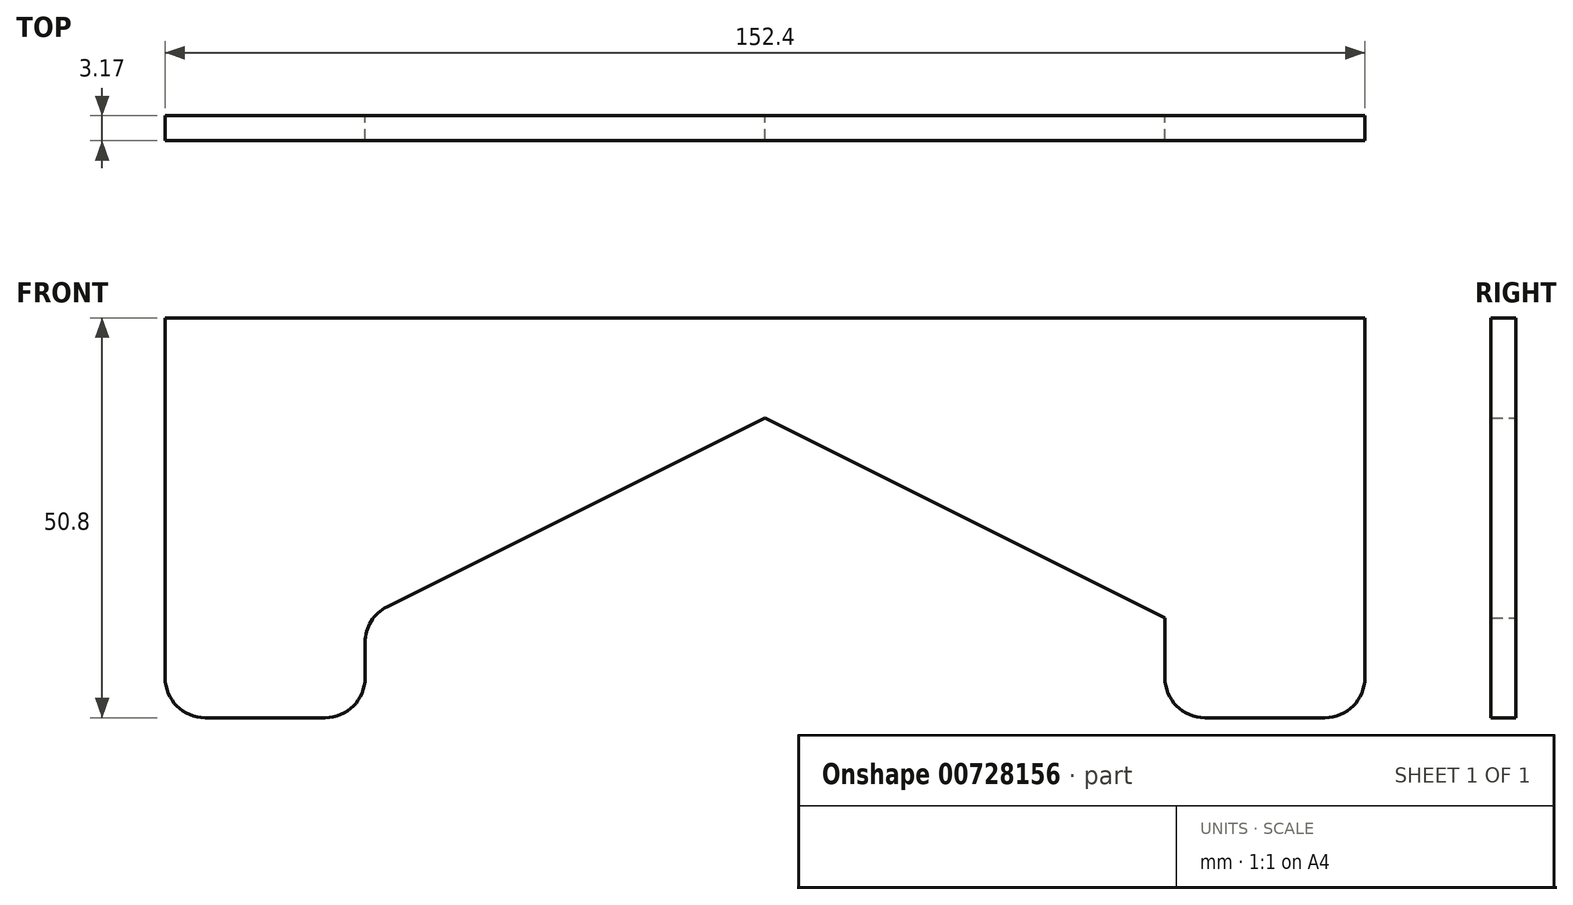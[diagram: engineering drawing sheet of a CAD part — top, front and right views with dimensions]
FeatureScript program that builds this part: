
annotation { "Feature Type Name" : "Feature", "Feature Type Description" : "" }
export const myFeature = defineFeature(function(context is Context, id is Id, definition is map)
    precondition{}
    {
        {
            var Q0;
            Q0=qCreatedBy(makeId("Front.planeOp"),FACE);
            var sketch = newSketch(context, id + "F0", { "sketchPlane" : qUnion([Q0])});
            skLineSegment(sketch, "E0", {"start": v(-107.22, 19.05) * mm, "end": v(-107.22, -31.75) * mm});
            skLineSegment(sketch, "E1", {"start": v(-107.22, -31.75) * mm, "end": v(45.18, -31.75) * mm});
            skLineSegment(sketch, "E2", {"start": v(45.18, -31.75) * mm, "end": v(45.18, 19.05) * mm});
            skLineSegment(sketch, "E3", {"start": v(45.18, 19.05) * mm, "end": v(-107.22, 19.05) * mm});
            skLineSegment(sketch, "E4", {"start": v(45.18, -6.35) * mm, "end": v(40.61, -6.35) * mm});
            skLineSegment(sketch, "E5", {"start": v(-31.02, -31.75) * mm, "end": v(-31.02, -6.35) * mm});
            skLineSegment(sketch, "E6", {"start": v(45.18, -31.75) * mm, "end": v(19.78, -31.75) * mm});
            skLineSegment(sketch, "E7.MirrorCS", {"start": v(-107.22, -31.75) * mm, "end": v(-81.82, -31.75) * mm});
            skLineSegment(sketch, "E8", {"start": v(-81.82, -31.75) * mm, "end": v(-81.82, -19.05) * mm});
            skLineSegment(sketch, "E9", {"start": v(-31.02, -6.35) * mm, "end": v(-31.02, 6.35) * mm});
            skLineSegment(sketch, "E10.MirrorCS", {"start": v(19.78, -31.75) * mm, "end": v(19.78, -19.05) * mm});
            skLineSegment(sketch, "E11", {"start": v(19.78, -19.05) * mm, "end": v(-31.02, 6.35) * mm});
            skLineSegment(sketch, "E12", {"start": v(-81.82, -19.05) * mm, "end": v(-31.02, 6.35) * mm});
            skSolve(sketch);
        }
        {
            var Q0;
            Q0=makeQuery(id+"F0.imprint","IMPRINT",FACE,{"disambiguationData":[TD([[makeQuery(id+"F0.imprint","IMPRINT",EDGE,{"derivedFrom":sQuery(id+"F0.wireOp",EDGE,"E0")}),1.0]])]});
            extrude(context, id + "F1", {"entities" : qUnion([Q0]), "depth" : 3.17 * mm, "offsetDistance" : 25.4 * mm});
        }
        {
            var Q0;
            Q0=makeQuery(id+"F1.opExtrude","SWEPT_EDGE",EDGE,{"disambiguationData":[OSD([sQuery(id+"F0.wireOp",EDGE,"fpcekhAr-Lv1i-5OIS-Z2bz-bTgvJPstimYA"),sQuery(id+"F0.wireOp",EDGE,"RrqWmqre-dpCM-NmQ2-ASZN-0iDyt0Ix4epU")])]});
            var Q1;
            Q1=makeQuery(id+"F1.opExtrude","SWEPT_EDGE",EDGE,{"disambiguationData":[OSD([sQuery(id+"F0.wireOp",EDGE,"E8"),sQuery(id+"F0.wireOp",EDGE,"UTAN609m-hBnK-2Cb8-olGW-VzUFbXciX6Di")])]});
            fillet(context, id + "F2", {"entities" : qUnion([Q0, Q1]), "radius" : 5.08 * mm, "tangentPropagation" : true, "allowEdgeOverflow" : false});
        }
        {
            var Q0;
            Q0=makeQuery(id+"F1.opExtrude","SWEPT_EDGE",EDGE,{"disambiguationData":[OSD([sQuery(id+"F0.wireOp",EDGE,"E1"),sQuery(id+"F0.wireOp",EDGE,"E7.MirrorCS"),sQuery(id+"F0.wireOp",EDGE,"E8")])]});
            var Q1;
            Q1=makeQuery(id+"F1.opExtrude","SWEPT_EDGE",EDGE,{"disambiguationData":[OSD([sQuery(id+"F0.wireOp",EDGE,"E1"),sQuery(id+"F0.wireOp",EDGE,"E6"),sQuery(id+"F0.wireOp",EDGE,"fpcekhAr-Lv1i-5OIS-Z2bz-bTgvJPstimYA")])]});
            fillet(context, id + "F3", {"entities" : qUnion([Q0, Q1]), "radius" : 5.08 * mm, "tangentPropagation" : true, "allowEdgeOverflow" : false});
        }
    });
